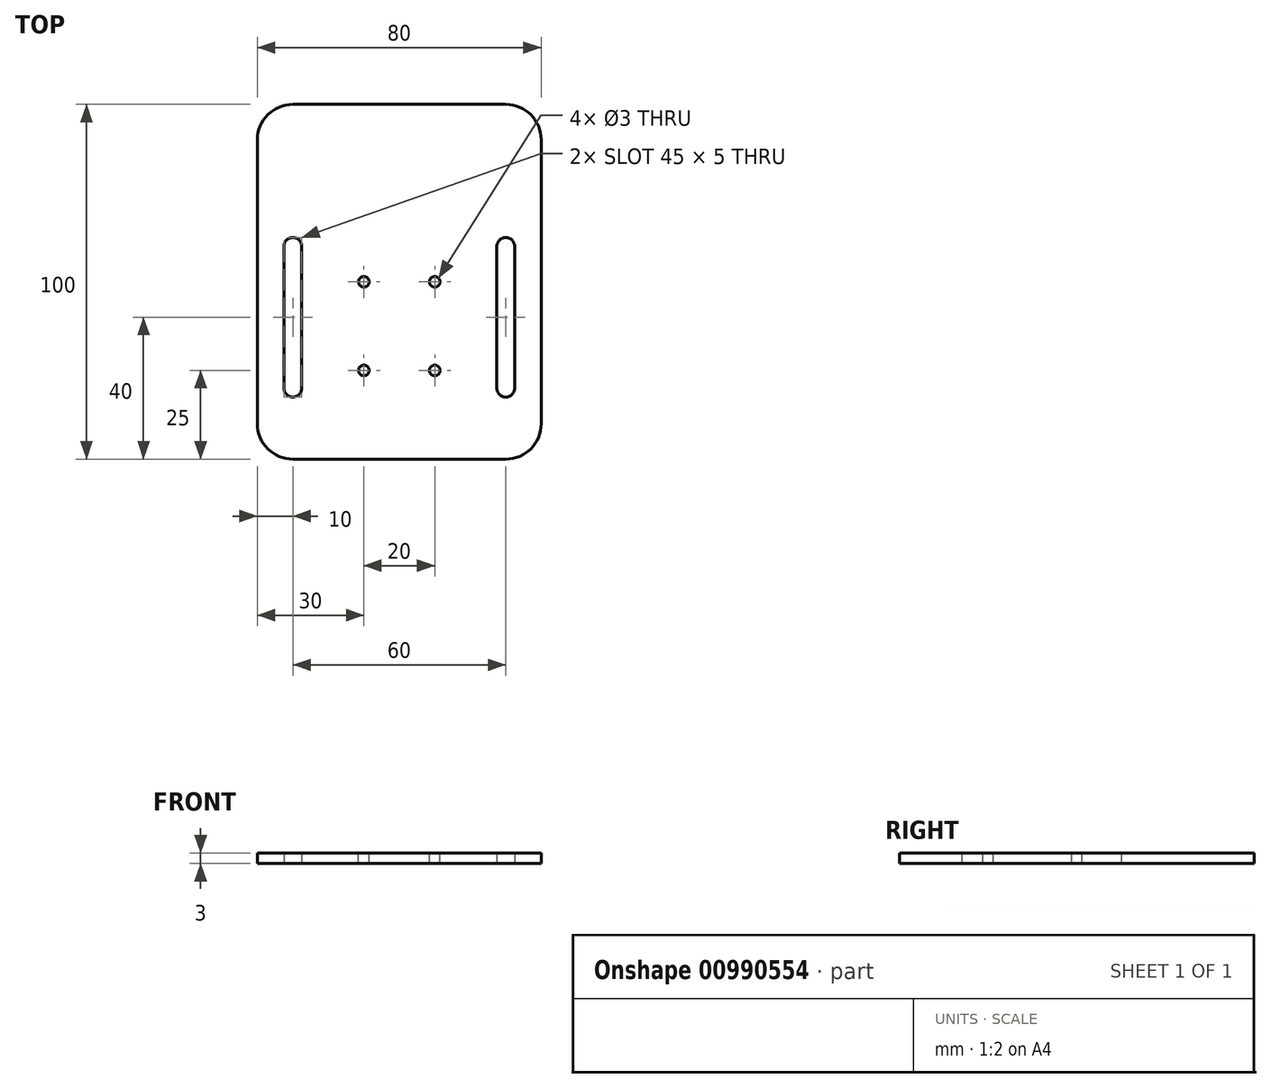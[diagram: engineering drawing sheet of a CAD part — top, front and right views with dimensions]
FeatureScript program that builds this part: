
annotation { "Feature Type Name" : "Feature", "Feature Type Description" : "" }
export const myFeature = defineFeature(function(context is Context, id is Id, definition is map)
    precondition{}
    {
        {
            var Q0;
            Q0=qCreatedBy(makeId("Top.planeOp"),FACE);
            var sketch = newSketch(context, id + "F0", { "sketchPlane" : qUnion([Q0])});
            skLineSegment(sketch, "E0.bottom", {"start": v(0, 0) * mm, "end": v(40, 0) * mm});
            skLineSegment(sketch, "E0.top", {"start": v(0, 100) * mm, "end": v(40, 100) * mm});
            skLineSegment(sketch, "E0.left", {"start": v(0, 0) * mm, "end": v(0, 100) * mm});
            skLineSegment(sketch, "E0.right", {"start": v(40, 0) * mm, "end": v(40, 100) * mm});
            skSolve(sketch);
        }
        {
            var Q0;
            Q0=makeQuery(id+"F0.imprint","IMPRINT",FACE,{"disambiguationData":[TD([[makeQuery(id+"F0.imprint","IMPRINT",EDGE,{"derivedFrom":sQuery(id+"F0.wireOp",EDGE,"E0.bottom")}),1.0]])]});
            extrude(context, id + "F1", {"entities" : qUnion([Q0]), "depth" : 3 * mm, "offsetDistance" : 25 * mm});
        }
        {
            var Q0;
            Q0=makeQuery(id+"F1.opExtrude","CAP_FACE",FACE,{"disambiguationData":[OSD([sQuery(id+"F0.wireOp",EDGE,"E0.bottom"),sQuery(id+"F0.wireOp",EDGE,"E0.top"),sQuery(id+"F0.wireOp",EDGE,"E0.left"),sQuery(id+"F0.wireOp",EDGE,"E0.right")])],"isStart":false});
            var sketch = newSketch(context, id + "F2", { "sketchPlane" : qUnion([Q0])});
            skLineSegment(sketch, "E1", {"start": v(10, 25) * mm, "end": v(10, 50) * mm});
            skSolve(sketch);
        }
        {
            var Q0;
            Q0=sQuery(id+"F2.wireOp",VERTEX,"E1.start");
            var Q1;
            Q1=sQuery(id+"F2.wireOp",VERTEX,"E1.end");
            var Q2;
            Q2=makeQuery(id+"F1.opExtrude","SWEPT_BODY",BODY,{"disambiguationData":[OSD([sQuery(id+"F0.wireOp",EDGE,"E0.bottom"),sQuery(id+"F0.wireOp",EDGE,"E0.top"),sQuery(id+"F0.wireOp",EDGE,"E0.left"),sQuery(id+"F0.wireOp",EDGE,"E0.right")])]});
            hole(context, id + "F3", {"style" : HoleStyle.SIMPLE, "endStyle" : HoleEndStyle.THROUGH, "holeDiameter" : 3 * mm, "majorDiameter" : 5 * mm, "isTappedThrough" : true, "tappedDepth" : 12 * mm, "tapClearance" : 3, "locations" : qUnion([Q0, Q1]), "scope" : qUnion([Q2])});
        }
        {
            var Q0;
            Q0=makeQuery(id+"F0.imprint","IMPRINT",FACE,{"disambiguationData":[TD([[makeQuery(id+"F0.imprint","IMPRINT",EDGE,{"derivedFrom":sQuery(id+"F0.wireOp",EDGE,"E0.bottom")}),1.0]])]});
            var sketch = newSketch(context, id + "F4", { "sketchPlane" : qUnion([Q0])});
            skLineSegment(sketch, "E2", {"start": v(30, 60) * mm, "end": v(30, 20) * mm});
            skLineSegment(sketch, "E3", {"start": v(30, 20) * mm, "end": v(30, 60) * mm});
            skArc(sketch, "E4.0.startCap", {"start": v(27.5, 60) * mm, "mid": v(30, 62.5) * mm, "end": v(32.5, 60) * mm});
            skArc(sketch, "E4.0.endCap", {"start": v(32.5, 20) * mm, "mid": v(30, 17.5) * mm, "end": v(27.5, 20) * mm});
            skLineSegment(sketch, "E4.0.left", {"start": v(32.5, 60) * mm, "end": v(32.5, 20) * mm});
            skLineSegment(sketch, "E4.0.right", {"start": v(27.5, 60) * mm, "end": v(27.5, 20) * mm});
            skSolve(sketch);
        }
        {
            var Q0;
            Q0 = qSketchRegion(id + "F4", true);
            extrude(context, id + "F5", {"entities" : qUnion([Q0]), "operationType" : NewBodyOperationType.REMOVE, "depth" : 77.02 * mm, "offsetDistance" : 25 * mm});
        }
        {
            var Q0;
            Q0=makeQuery(id+"F1.opExtrude","SWEPT_EDGE",EDGE,{"disambiguationData":[OSD([sQuery(id+"F0.wireOp",EDGE,"E0.bottom"),sQuery(id+"F0.wireOp",EDGE,"E0.right")])]});
            var Q1;
            Q1=makeQuery(id+"F1.opExtrude","SWEPT_EDGE",EDGE,{"disambiguationData":[OSD([sQuery(id+"F0.wireOp",EDGE,"E0.top"),sQuery(id+"F0.wireOp",EDGE,"E0.right")])]});
            fillet(context, id + "F6", {"entities" : qUnion([Q0, Q1]), "radius" : 10 * mm, "tangentPropagation" : true, "allowEdgeOverflow" : false});
        }
        {
            var Q0;
            Q0=makeQuery(id+"F1.opExtrude","SWEPT_BODY",BODY,{"disambiguationData":[OSD([sQuery(id+"F0.wireOp",EDGE,"E0.bottom"),sQuery(id+"F0.wireOp",EDGE,"E0.top"),sQuery(id+"F0.wireOp",EDGE,"E0.left"),sQuery(id+"F0.wireOp",EDGE,"E0.right")])]});
            var Q1;
            Q1=qCreatedBy(makeId("Right.planeOp"),FACE);
            mirror(context, id + "F7", {"operationType" : NewBodyOperationType.ADD, "entities" : qUnion([Q0]), "mirrorPlane" : qUnion([Q1])});
        }
    });
